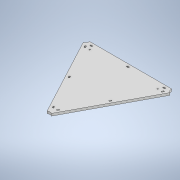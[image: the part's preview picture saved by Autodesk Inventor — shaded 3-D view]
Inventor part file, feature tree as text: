
AUTODESK INVENTOR PART (.ipt)
format: ipt  version: 2020 (Build 240168000, 168)  size: 154,112 bytes
history: native  units: in
note: dims shown in document units (in); Inventor stores cm internally (conversion verified against a paired STEP export)
features: extrude x1, sketch x1
ambient origin geometry x8: Origin, YZ Plane, XZ Plane, XY Plane, X Axis, Y Axis, Z Axis, Center Point
bodies: Solid1 (feature_tree)
feature tree (2):
  extrude  "Extrusion1"  [1 undecoded]
  sketch  "Sketch1"  dims[d0=0.1575in d1=0.0in]
note: 1 required parameter value undecoded (feature->parameter linkage not recoverable at this tier; creation-order binding heuristic only, values carry confidence <= 0.55)
